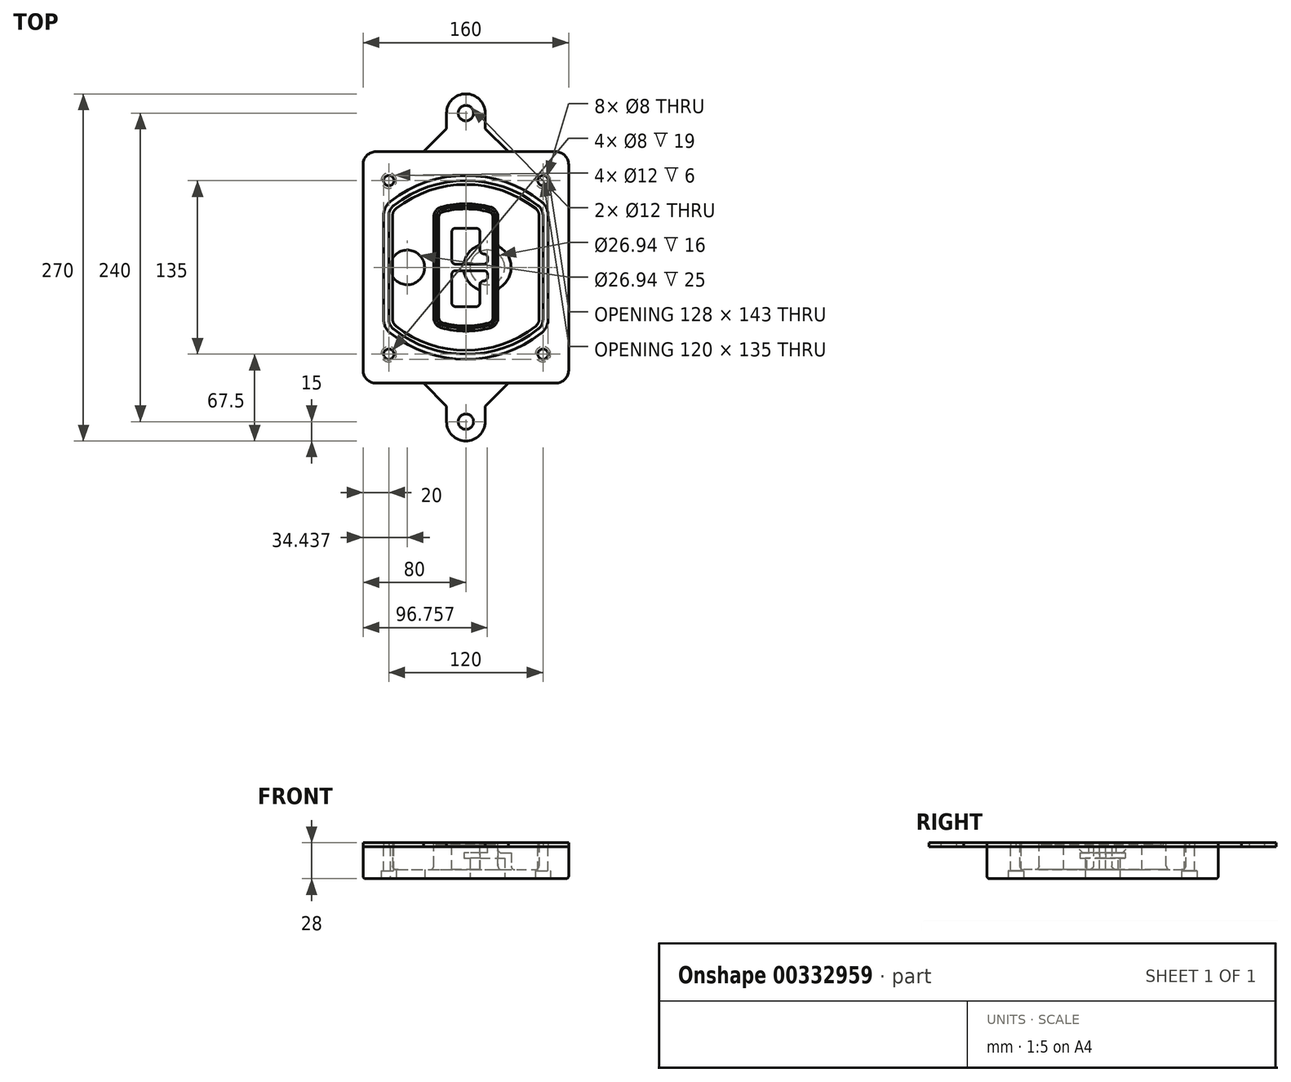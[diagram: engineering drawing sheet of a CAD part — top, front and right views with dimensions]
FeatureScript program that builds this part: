
annotation { "Feature Type Name" : "Feature", "Feature Type Description" : "" }
export const myFeature = defineFeature(function(context is Context, id is Id, definition is map)
    precondition{}
    {
        {
            var Q0;
            Q0=qCreatedBy(makeId("Top.planeOp"),FACE);
            var sketch = newSketch(context, id + "F0", { "sketchPlane" : qUnion([Q0])});
            skPoint(sketch, "E0.rect.middle", {"position": v(0, 0) * mm});
            skLineSegment(sketch, "E1.bottom", {"start": v(-70, -90) * mm, "end": v(70, -90) * mm});
            skLineSegment(sketch, "E1.top", {"start": v(-70, 90) * mm, "end": v(70, 90) * mm});
            skLineSegment(sketch, "E1.left", {"start": v(-80, -80) * mm, "end": v(-80, 80) * mm});
            skLineSegment(sketch, "E1.right", {"start": v(80, -80) * mm, "end": v(80, 80) * mm});
            skLineSegment(sketch, "E2", {"start": v(-80, 90) * mm, "end": v(80, -90) * mm, "construction": true});
            skLineSegment(sketch, "E3", {"start": v(80, 90) * mm, "end": v(-80, -90) * mm, "construction": true});
            skCircle(sketch, "E4", {"center": v(-60, 67.5) * mm, "radius": 4 * mm});
            skCircle(sketch, "E5", {"center": v(60, 67.5) * mm, "radius": 4 * mm});
            skCircle(sketch, "E6", {"center": v(60, -67.5) * mm, "radius": 4 * mm});
            skCircle(sketch, "E7", {"center": v(-60, -67.5) * mm, "radius": 4 * mm});
            skLineSegment(sketch, "E8", {"start": v(-60, 67.5) * mm, "end": v(60, 67.5) * mm, "construction": true});
            skLineSegment(sketch, "E9", {"start": v(60, 67.5) * mm, "end": v(60, -67.5) * mm, "construction": true});
            skLineSegment(sketch, "E10", {"start": v(60, -67.5) * mm, "end": v(-60, -67.5) * mm, "construction": true});
            skLineSegment(sketch, "E11", {"start": v(-60, -67.5) * mm, "end": v(-60, 67.5) * mm, "construction": true});
            skLineSegment(sketch, "E12", {"start": v(-60, 40.3) * mm, "end": v(-60, -40.3) * mm});
            skLineSegment(sketch, "E13", {"start": v(60, 40.3) * mm, "end": v(60, -40.3) * mm});
            skArc(sketch, "E14", {"start": v(56.15, 48.18) * mm, "mid": v(0, 67.5) * mm, "end": v(-56.15, 48.18) * mm});
            skArc(sketch, "E15", {"start": v(-56.15, -48.18) * mm, "mid": v(0, -67.5) * mm, "end": v(56.15, -48.18) * mm});
            skLineSegment(sketch, "E16", {"start": v(-60, 0) * mm, "end": v(60, 0) * mm, "construction": true});
            skPoint(sketch, "E17.visualSharp", {"position": v(-60, -45) * mm});
            skArc(sketch, "E17.filletArc", {"start": v(-60, -40.3) * mm, "mid": v(-58.99, -44.68) * mm, "end": v(-56.15, -48.18) * mm});
            skPoint(sketch, "E18.visualSharp", {"position": v(-60, 45) * mm});
            skArc(sketch, "E18.filletArc", {"start": v(-56.15, 48.18) * mm, "mid": v(-58.99, 44.68) * mm, "end": v(-60, 40.3) * mm});
            skPoint(sketch, "E19.visualSharp", {"position": v(60, 45) * mm});
            skArc(sketch, "E19.filletArc", {"start": v(60, 40.3) * mm, "mid": v(58.99, 44.68) * mm, "end": v(56.15, 48.18) * mm});
            skPoint(sketch, "E20.visualSharp", {"position": v(60, -45) * mm});
            skArc(sketch, "E20.filletArc", {"start": v(56.15, -48.18) * mm, "mid": v(58.99, -44.68) * mm, "end": v(60, -40.3) * mm});
            skPoint(sketch, "E21.visualSharp", {"position": v(-80, 90) * mm});
            skArc(sketch, "E21.filletArc", {"start": v(-70, 90) * mm, "mid": v(-77.07, 87.07) * mm, "end": v(-80, 80) * mm});
            skPoint(sketch, "E22.visualSharp", {"position": v(80, 90) * mm});
            skArc(sketch, "E22.filletArc", {"start": v(80, 80) * mm, "mid": v(77.07, 87.07) * mm, "end": v(70, 90) * mm});
            skPoint(sketch, "E23.visualSharp", {"position": v(80, -90) * mm});
            skArc(sketch, "E23.filletArc", {"start": v(70, -90) * mm, "mid": v(77.07, -87.07) * mm, "end": v(80, -80) * mm});
            skPoint(sketch, "E24.visualSharp", {"position": v(-80, -90) * mm});
            skArc(sketch, "E24.filletArc", {"start": v(-80, -80) * mm, "mid": v(-77.07, -87.07) * mm, "end": v(-70, -90) * mm});
            skArc(sketch, "E25.0", {"start": v(57, 40.3) * mm, "mid": v(56.3, 43.36) * mm, "end": v(54.3, 45.81) * mm});
            skLineSegment(sketch, "E25.1", {"start": v(57, 40.3) * mm, "end": v(57, -40.3) * mm});
            skArc(sketch, "E25.2", {"start": v(54.3, -45.81) * mm, "mid": v(56.3, -43.36) * mm, "end": v(57, -40.3) * mm});
            skArc(sketch, "E25.3", {"start": v(-54.3, -45.81) * mm, "mid": v(0, -64.5) * mm, "end": v(54.3, -45.81) * mm});
            skArc(sketch, "E25.4", {"start": v(-57, -40.3) * mm, "mid": v(-56.3, -43.36) * mm, "end": v(-54.3, -45.81) * mm});
            skArc(sketch, "E25.5", {"start": v(54.3, 45.81) * mm, "mid": v(0, 64.5) * mm, "end": v(-54.3, 45.81) * mm});
            skLineSegment(sketch, "E25.6", {"start": v(-57, 40.3) * mm, "end": v(-57, -40.3) * mm});
            skArc(sketch, "E25.7", {"start": v(-54.3, 45.81) * mm, "mid": v(-56.3, 43.36) * mm, "end": v(-57, 40.3) * mm});
            skArc(sketch, "E26.0", {"start": v(-58.62, 51.33) * mm, "mid": v(-62.58, 46.43) * mm, "end": v(-64, 40.3) * mm});
            skArc(sketch, "E26.1", {"start": v(58.62, 51.33) * mm, "mid": v(0, 71.5) * mm, "end": v(-58.62, 51.33) * mm});
            skArc(sketch, "E26.2", {"start": v(64, 40.3) * mm, "mid": v(62.58, 46.43) * mm, "end": v(58.62, 51.33) * mm});
            skLineSegment(sketch, "E26.3", {"start": v(64, 40.3) * mm, "end": v(64, -40.3) * mm});
            skArc(sketch, "E26.4", {"start": v(58.62, -51.33) * mm, "mid": v(62.58, -46.43) * mm, "end": v(64, -40.3) * mm});
            skLineSegment(sketch, "E26.5", {"start": v(-64, 40.3) * mm, "end": v(-64, -40.3) * mm});
            skArc(sketch, "E26.6", {"start": v(-58.62, -51.33) * mm, "mid": v(0, -71.5) * mm, "end": v(58.62, -51.33) * mm});
            skArc(sketch, "E26.7", {"start": v(-64, -40.3) * mm, "mid": v(-62.58, -46.43) * mm, "end": v(-58.62, -51.33) * mm});
            skSolve(sketch);
        }
        {
            var Q0;
            Q0=makeQuery(id+"F0.imprint","IMPRINT",FACE,{"disambiguationData":[TD([[makeQuery(id+"F0.imprint","IMPRINT",EDGE,{"derivedFrom":sQuery(id+"F0.wireOp",EDGE,"E1.bottom")}),1.0]])]});
            var Q1;
            Q1=makeQuery(id+"F0.imprint","IMPRINT",FACE,{"disambiguationData":[TD([[makeQuery(id+"F0.imprint","IMPRINT",EDGE,{"derivedFrom":sQuery(id+"F0.wireOp",EDGE,"E12")}),1.0]])]});
            var Q2;
            Q2=makeQuery(id+"F0.imprint","IMPRINT",FACE,{"disambiguationData":[TD([[makeQuery(id+"F0.imprint","IMPRINT",EDGE,{"derivedFrom":sQuery(id+"F0.wireOp",EDGE,"E25.0")}),1.0]])]});
            var Q3;
            Q3=makeQuery(id+"F0.imprint","IMPRINT",FACE,{"disambiguationData":[TD([[makeQuery(id+"F0.imprint","IMPRINT",EDGE,{"derivedFrom":sQuery(id+"F0.wireOp",EDGE,"E12")}),-1.0]])]});
            extrude(context, id + "F1", {"entities" : qUnion([Q0, Q1, Q2, Q3]), "oppositeDirection" : true, "depth" : 25 * mm});
        }
        {
            var Q0;
            Q0=makeQuery(id+"F0.imprint","IMPRINT",FACE,{"disambiguationData":[TD([[makeQuery(id+"F0.imprint","IMPRINT",EDGE,{"derivedFrom":sQuery(id+"F0.wireOp",EDGE,"E12")}),1.0]])]});
            extrude(context, id + "F2", {"entities" : qUnion([Q0]), "operationType" : NewBodyOperationType.ADD, "depth" : 3 * mm});
        }
        {
            var Q0;
            Q0=makeQuery(id+"F0.imprint","IMPRINT",FACE,{"disambiguationData":[TD([[makeQuery(id+"F0.imprint","IMPRINT",EDGE,{"derivedFrom":sQuery(id+"F0.wireOp",EDGE,"E25.0")}),1.0]])]});
            extrude(context, id + "F3", {"entities" : qUnion([Q0]), "operationType" : NewBodyOperationType.REMOVE, "oppositeDirection" : true, "depth" : 18 * mm});
        }
        {
            var Q0;
            Q0=makeQuery(id+"F2.opExtrude","CAP_FACE",FACE,{"disambiguationData":[OSD([sQuery(id+"F0.wireOp",EDGE,"E12"),sQuery(id+"F0.wireOp",EDGE,"E13"),sQuery(id+"F0.wireOp",EDGE,"E14"),sQuery(id+"F0.wireOp",EDGE,"E15"),sQuery(id+"F0.wireOp",EDGE,"E17.filletArc"),sQuery(id+"F0.wireOp",EDGE,"E18.filletArc"),sQuery(id+"F0.wireOp",EDGE,"E19.filletArc"),sQuery(id+"F0.wireOp",EDGE,"E20.filletArc"),sQuery(id+"F0.wireOp",EDGE,"E25.0"),sQuery(id+"F0.wireOp",EDGE,"E25.1"),sQuery(id+"F0.wireOp",EDGE,"E25.2"),sQuery(id+"F0.wireOp",EDGE,"E25.3"),sQuery(id+"F0.wireOp",EDGE,"E25.4"),sQuery(id+"F0.wireOp",EDGE,"E25.5"),sQuery(id+"F0.wireOp",EDGE,"E25.6"),sQuery(id+"F0.wireOp",EDGE,"E25.7")])],"isStart":false});
            var sketch = newSketch(context, id + "F4", { "sketchPlane" : qUnion([Q0])});
            skArc(sketch, "E27.0", {"start": v(-19.08, -46.97) * mm, "mid": v(0, -49.5) * mm, "end": v(19.08, -46.97) * mm});
            skArc(sketch, "E28.0", {"start": v(19.08, 46.97) * mm, "mid": v(0, 49.5) * mm, "end": v(-19.08, 46.97) * mm});
            skLineSegment(sketch, "E29", {"start": v(-25, 39.25) * mm, "end": v(-25, -39.25) * mm});
            skLineSegment(sketch, "E30", {"start": v(25, 39.25) * mm, "end": v(25, -39.25) * mm});
            skLineSegment(sketch, "E31", {"start": v(-25, 45.1) * mm, "end": v(25, 45.1) * mm, "construction": true});
            skLineSegment(sketch, "E32", {"start": v(-25, -45.1) * mm, "end": v(25, -45.1) * mm, "construction": true});
            skPoint(sketch, "E33.visualSharp", {"position": v(-25, 45.1) * mm});
            skArc(sketch, "E33.filletArc", {"start": v(-19.08, 46.97) * mm, "mid": v(-23.35, 44.11) * mm, "end": v(-25, 39.25) * mm});
            skPoint(sketch, "E34.visualSharp", {"position": v(25, 45.1) * mm});
            skArc(sketch, "E34.filletArc", {"start": v(25, 39.25) * mm, "mid": v(23.35, 44.11) * mm, "end": v(19.08, 46.97) * mm});
            skPoint(sketch, "E35.visualSharp", {"position": v(25, -45.1) * mm});
            skArc(sketch, "E35.filletArc", {"start": v(19.08, -46.97) * mm, "mid": v(23.35, -44.11) * mm, "end": v(25, -39.25) * mm});
            skPoint(sketch, "E36.visualSharp", {"position": v(-25, -45.1) * mm});
            skArc(sketch, "E36.filletArc", {"start": v(-25, -39.25) * mm, "mid": v(-23.35, -44.11) * mm, "end": v(-19.08, -46.97) * mm});
            skArc(sketch, "E37.0", {"start": v(54.3, 45.81) * mm, "mid": v(0, 64.5) * mm, "end": v(-54.3, 45.81) * mm});
            skArc(sketch, "E37.1", {"start": v(-54.3, 45.81) * mm, "mid": v(-56.3, 43.36) * mm, "end": v(-57, 40.3) * mm});
            skLineSegment(sketch, "E37.2", {"start": v(-57, 40.3) * mm, "end": v(-57, -40.3) * mm});
            skArc(sketch, "E37.3", {"start": v(-57, -40.3) * mm, "mid": v(-56.3, -43.36) * mm, "end": v(-54.3, -45.81) * mm});
            skArc(sketch, "E37.4", {"start": v(-54.3, -45.81) * mm, "mid": v(0, -64.5) * mm, "end": v(54.3, -45.81) * mm});
            skArc(sketch, "E37.5", {"start": v(54.3, -45.81) * mm, "mid": v(56.3, -43.36) * mm, "end": v(57, -40.3) * mm});
            skLineSegment(sketch, "E37.6", {"start": v(57, 40.3) * mm, "end": v(57, -40.3) * mm});
            skArc(sketch, "E37.7", {"start": v(57, 40.3) * mm, "mid": v(56.3, 43.36) * mm, "end": v(54.3, 45.81) * mm});
            skLineSegment(sketch, "E38.0", {"start": v(23, 39.25) * mm, "end": v(23, -39.25) * mm});
            skArc(sketch, "E38.1", {"start": v(18.56, -45.04) * mm, "mid": v(21.76, -42.9) * mm, "end": v(23, -39.25) * mm});
            skArc(sketch, "E38.2", {"start": v(-18.56, -45.04) * mm, "mid": v(0, -47.5) * mm, "end": v(18.56, -45.04) * mm});
            skArc(sketch, "E38.3", {"start": v(-23, -39.25) * mm, "mid": v(-21.76, -42.9) * mm, "end": v(-18.56, -45.04) * mm});
            skLineSegment(sketch, "E38.4", {"start": v(-23, 39.25) * mm, "end": v(-23, -39.25) * mm});
            skArc(sketch, "E38.5", {"start": v(23, 39.25) * mm, "mid": v(21.76, 42.9) * mm, "end": v(18.56, 45.04) * mm});
            skArc(sketch, "E38.6", {"start": v(-18.56, 45.04) * mm, "mid": v(-21.76, 42.9) * mm, "end": v(-23, 39.25) * mm});
            skArc(sketch, "E38.7", {"start": v(18.56, 45.04) * mm, "mid": v(0, 47.5) * mm, "end": v(-18.56, 45.04) * mm});
            skArc(sketch, "E39.0", {"start": v(21, 39.25) * mm, "mid": v(20.18, 41.68) * mm, "end": v(18.04, 43.1) * mm});
            skLineSegment(sketch, "E39.1", {"start": v(21, 39.25) * mm, "end": v(21, -39.25) * mm});
            skArc(sketch, "E39.2", {"start": v(18.04, -43.1) * mm, "mid": v(20.18, -41.68) * mm, "end": v(21, -39.25) * mm});
            skArc(sketch, "E39.3", {"start": v(-18.04, -43.1) * mm, "mid": v(0, -45.5) * mm, "end": v(18.04, -43.1) * mm});
            skArc(sketch, "E39.4", {"start": v(-21, -39.25) * mm, "mid": v(-20.18, -41.68) * mm, "end": v(-18.04, -43.1) * mm});
            skArc(sketch, "E39.5", {"start": v(18.04, 43.1) * mm, "mid": v(0, 45.5) * mm, "end": v(-18.04, 43.1) * mm});
            skLineSegment(sketch, "E39.6", {"start": v(-21, 39.25) * mm, "end": v(-21, -39.25) * mm});
            skArc(sketch, "E39.7", {"start": v(-18.04, 43.1) * mm, "mid": v(-20.18, 41.68) * mm, "end": v(-21, 39.25) * mm});
            skLineSegment(sketch, "E40", {"start": v(-25, 0) * mm, "end": v(25, 0) * mm, "construction": true});
            skLineSegment(sketch, "E41", {"start": v(-11, 5.5) * mm, "end": v(-11, 27.5) * mm});
            skLineSegment(sketch, "E42", {"start": v(-8, 30.5) * mm, "end": v(8, 30.5) * mm});
            skLineSegment(sketch, "E43", {"start": v(11, 27.5) * mm, "end": v(11, 13.5) * mm});
            skLineSegment(sketch, "E44", {"start": v(14, 10.5) * mm, "end": v(14, 10.5) * mm});
            skLineSegment(sketch, "E45", {"start": v(17, 7.5) * mm, "end": v(17, 5.5) * mm});
            skLineSegment(sketch, "E46", {"start": v(14, 2.5) * mm, "end": v(-8, 2.5) * mm});
            skPoint(sketch, "E47.visualSharp", {"position": v(-11, 30.5) * mm});
            skArc(sketch, "E47.filletArc", {"start": v(-8, 30.5) * mm, "mid": v(-10.12, 29.62) * mm, "end": v(-11, 27.5) * mm});
            skPoint(sketch, "E48.visualSharp", {"position": v(11, 30.5) * mm});
            skArc(sketch, "E48.filletArc", {"start": v(11, 27.5) * mm, "mid": v(10.12, 29.62) * mm, "end": v(8, 30.5) * mm});
            skPoint(sketch, "E49.visualSharp", {"position": v(11, 10.5) * mm});
            skArc(sketch, "E49.filletArc", {"start": v(11, 13.5) * mm, "mid": v(11.88, 11.38) * mm, "end": v(14, 10.5) * mm});
            skPoint(sketch, "E50.visualSharp", {"position": v(17, 10.5) * mm});
            skArc(sketch, "E50.filletArc", {"start": v(17, 7.5) * mm, "mid": v(16.12, 9.62) * mm, "end": v(14, 10.5) * mm});
            skPoint(sketch, "E51.visualSharp", {"position": v(17, 2.5) * mm});
            skArc(sketch, "E51.filletArc", {"start": v(14, 2.5) * mm, "mid": v(16.12, 3.38) * mm, "end": v(17, 5.5) * mm});
            skPoint(sketch, "E52.visualSharp", {"position": v(-11, 2.5) * mm});
            skArc(sketch, "E52.filletArc", {"start": v(-11, 5.5) * mm, "mid": v(-10.12, 3.38) * mm, "end": v(-8, 2.5) * mm});
            skLineSegment(sketch, "E53.0.MirrorCS", {"start": v(14, -2.5) * mm, "end": v(-8, -2.5) * mm});
            skArc(sketch, "E54.0.MirrorCS", {"start": v(-11, -5.5) * mm, "mid": v(-10.12, -3.38) * mm, "end": v(-8, -2.5) * mm});
            skLineSegment(sketch, "E55.0.MirrorCS", {"start": v(-11, -5.5) * mm, "end": v(-11, -27.5) * mm});
            skArc(sketch, "E56.0.MirrorCS", {"start": v(-8, -30.5) * mm, "mid": v(-10.12, -29.62) * mm, "end": v(-11, -27.5) * mm});
            skLineSegment(sketch, "E57.0.MirrorCS", {"start": v(-8, -30.5) * mm, "end": v(8, -30.5) * mm});
            skArc(sketch, "E58.0.MirrorCS", {"start": v(11, -27.5) * mm, "mid": v(10.12, -29.62) * mm, "end": v(8, -30.5) * mm});
            skLineSegment(sketch, "E59.0.MirrorCS", {"start": v(11, -27.5) * mm, "end": v(11, -13.5) * mm});
            skArc(sketch, "E60.0.MirrorCS", {"start": v(11, -13.5) * mm, "mid": v(11.88, -11.38) * mm, "end": v(14, -10.5) * mm});
            skArc(sketch, "E61.0.MirrorCS", {"start": v(17, -7.5) * mm, "mid": v(16.12, -9.62) * mm, "end": v(14, -10.5) * mm});
            skLineSegment(sketch, "E62.0.MirrorCS", {"start": v(17, -7.5) * mm, "end": v(17, -5.5) * mm});
            skArc(sketch, "E63.0.MirrorCS", {"start": v(14, -2.5) * mm, "mid": v(16.12, -3.38) * mm, "end": v(17, -5.5) * mm});
            skSolve(sketch);
        }
        {
            var Q0;
            Q0=makeQuery(id+"F4.imprint","IMPRINT",FACE,{"disambiguationData":[TD([[makeQuery(id+"F4.imprint","IMPRINT",EDGE,{"derivedFrom":sQuery(id+"F4.wireOp",EDGE,"E27.0")}),1.0]])]});
            var Q1;
            Q1=makeQuery(id+"F4.imprint","IMPRINT",FACE,{"disambiguationData":[TD([[makeQuery(id+"F4.imprint","IMPRINT",EDGE,{"derivedFrom":sQuery(id+"F4.wireOp",EDGE,"E38.0")}),-1.0]])]});
            var Q2;
            Q2=makeQuery(id+"F4.imprint","IMPRINT",FACE,{"disambiguationData":[TD([[makeQuery(id+"F4.imprint","IMPRINT",EDGE,{"derivedFrom":sQuery(id+"F4.wireOp",EDGE,"E39.0")}),1.0]])]});
            extrude(context, id + "F5", {"entities" : qUnion([Q0, Q1, Q2]), "operationType" : NewBodyOperationType.ADD, "endBound" : BoundingType.UP_TO_NEXT, "oppositeDirection" : true, "depth" : 25 * mm});
        }
        {
            var Q0;
            Q0=makeQuery(id+"F4.imprint","IMPRINT",FACE,{"disambiguationData":[TD([[makeQuery(id+"F4.imprint","IMPRINT",EDGE,{"derivedFrom":sQuery(id+"F4.wireOp",EDGE,"E38.0")}),-1.0]])]});
            extrude(context, id + "F6", {"entities" : qUnion([Q0]), "operationType" : NewBodyOperationType.REMOVE, "oppositeDirection" : true, "depth" : 2 * mm});
        }
        {
            var Q0;
            Q0=makeQuery(id+"F1.opExtrude","CAP_FACE",FACE,{"disambiguationData":[OSD([sQuery(id+"F0.wireOp",EDGE,"E1.bottom"),sQuery(id+"F0.wireOp",EDGE,"E1.top"),sQuery(id+"F0.wireOp",EDGE,"E1.left"),sQuery(id+"F0.wireOp",EDGE,"E1.right"),sQuery(id+"F0.wireOp",EDGE,"E4"),sQuery(id+"F0.wireOp",EDGE,"E5"),sQuery(id+"F0.wireOp",EDGE,"E6"),sQuery(id+"F0.wireOp",EDGE,"E7"),sQuery(id+"F0.wireOp",EDGE,"E21.filletArc"),sQuery(id+"F0.wireOp",EDGE,"E22.filletArc"),sQuery(id+"F0.wireOp",EDGE,"E23.filletArc"),sQuery(id+"F0.wireOp",EDGE,"E24.filletArc")])],"isStart":false});
            var sketch = newSketch(context, id + "F7", { "sketchPlane" : qUnion([Q0])});
            skCircle(sketch, "E64", {"center": v(16.76, 0) * mm, "radius": 13.47 * mm});
            skCircle(sketch, "E65", {"center": v(-45.56, 0) * mm, "radius": 13.47 * mm});
            skLineSegment(sketch, "E66", {"start": v(80, 0) * mm, "end": v(-80, 0) * mm});
            skCircle(sketch, "E67", {"center": v(16.76, 0) * mm, "radius": 18.47 * mm});
            skCircle(sketch, "E68", {"center": v(60, -67.5) * mm, "radius": 6 * mm});
            skCircle(sketch, "E69", {"center": v(-60, -67.5) * mm, "radius": 6 * mm});
            skCircle(sketch, "E70", {"center": v(-60, 67.5) * mm, "radius": 6 * mm});
            skCircle(sketch, "E71", {"center": v(60, 67.5) * mm, "radius": 6 * mm});
            skSolve(sketch);
        }
        {
            var Q0;
            {var subQ1=sQuery(id+"F7.wireOp",EDGE,"E66");var subQ4=sQuery(id+"F7.wireOp",EDGE,"E64");var subQ6=makeQuery(id+"F7.imprint","INTERSECT",VERTEX,{"disambiguationData":[OD(0.0)],"derivedFrom":[subQ4,subQ1]});Q0=makeQuery(id+"F7.imprint","IMPRINT",FACE,{"disambiguationData":[TD([[makeQuery(id+"F7.imprint","IMPRINT",EDGE,{"disambiguationData":[TD([[subQ6,-1.0]])],"derivedFrom":subQ4}),-1.0]])]});}
            var Q1;
            {var subQ0=sQuery(id+"F7.wireOp",EDGE,"E66");var subQ1=sQuery(id+"F7.wireOp",EDGE,"E64");var subQ3=makeQuery(id+"F7.imprint","INTERSECT",VERTEX,{"disambiguationData":[OD(0.0)],"derivedFrom":[subQ1,subQ0]});Q1=makeQuery(id+"F7.imprint","IMPRINT",FACE,{"disambiguationData":[TD([[makeQuery(id+"F7.imprint","IMPRINT",EDGE,{"disambiguationData":[TD([[subQ3,-1.0]])],"derivedFrom":subQ1}),1.0]])]});}
            var Q2;
            {var subQ0=sQuery(id+"F7.wireOp",EDGE,"E66");var subQ1=sQuery(id+"F7.wireOp",EDGE,"E64");var subQ3=makeQuery(id+"F7.imprint","INTERSECT",VERTEX,{"disambiguationData":[OD(0.0)],"derivedFrom":[subQ1,subQ0]});Q2=makeQuery(id+"F7.imprint","IMPRINT",FACE,{"disambiguationData":[TD([[makeQuery(id+"F7.imprint","IMPRINT",EDGE,{"disambiguationData":[TD([[subQ3,1.0]])],"derivedFrom":subQ1}),1.0]])]});}
            var Q3;
            {var subQ1=sQuery(id+"F7.wireOp",EDGE,"E66");var subQ4=sQuery(id+"F7.wireOp",EDGE,"E64");var subQ6=makeQuery(id+"F7.imprint","INTERSECT",VERTEX,{"disambiguationData":[OD(0.0)],"derivedFrom":[subQ4,subQ1]});Q3=makeQuery(id+"F7.imprint","IMPRINT",FACE,{"disambiguationData":[TD([[makeQuery(id+"F7.imprint","IMPRINT",EDGE,{"disambiguationData":[TD([[subQ6,1.0]])],"derivedFrom":subQ4}),-1.0]])]});}
            extrude(context, id + "F8", {"entities" : qUnion([Q0, Q1, Q2, Q3]), "operationType" : NewBodyOperationType.ADD, "oppositeDirection" : true, "depth" : 20 * mm});
        }
        {
            var Q0;
            {var subQ0=sQuery(id+"F7.wireOp",EDGE,"E66");var subQ1=sQuery(id+"F7.wireOp",EDGE,"E64");var subQ3=makeQuery(id+"F7.imprint","INTERSECT",VERTEX,{"disambiguationData":[OD(0.0)],"derivedFrom":[subQ1,subQ0]});Q0=makeQuery(id+"F7.imprint","IMPRINT",FACE,{"disambiguationData":[TD([[makeQuery(id+"F7.imprint","IMPRINT",EDGE,{"disambiguationData":[TD([[subQ3,-1.0]])],"derivedFrom":subQ1}),1.0]])]});}
            var Q1;
            {var subQ0=sQuery(id+"F7.wireOp",EDGE,"E66");var subQ1=sQuery(id+"F7.wireOp",EDGE,"E64");var subQ3=makeQuery(id+"F7.imprint","INTERSECT",VERTEX,{"disambiguationData":[OD(0.0)],"derivedFrom":[subQ1,subQ0]});Q1=makeQuery(id+"F7.imprint","IMPRINT",FACE,{"disambiguationData":[TD([[makeQuery(id+"F7.imprint","IMPRINT",EDGE,{"disambiguationData":[TD([[subQ3,1.0]])],"derivedFrom":subQ1}),1.0]])]});}
            extrude(context, id + "F9", {"entities" : qUnion([Q0, Q1]), "operationType" : NewBodyOperationType.REMOVE, "oppositeDirection" : true, "depth" : 16 * mm});
        }
        {
            var Q0;
            {var subQ0=sQuery(id+"F7.wireOp",EDGE,"E66");var subQ1=sQuery(id+"F7.wireOp",EDGE,"E65");var subQ3=makeQuery(id+"F7.imprint","INTERSECT",VERTEX,{"disambiguationData":[OD(0.0)],"derivedFrom":[subQ1,subQ0]});Q0=makeQuery(id+"F7.imprint","IMPRINT",FACE,{"disambiguationData":[TD([[makeQuery(id+"F7.imprint","IMPRINT",EDGE,{"disambiguationData":[TD([[subQ3,-1.0]])],"derivedFrom":subQ1}),1.0]])]});}
            var Q1;
            {var subQ0=sQuery(id+"F7.wireOp",EDGE,"E66");var subQ1=sQuery(id+"F7.wireOp",EDGE,"E65");var subQ3=makeQuery(id+"F7.imprint","INTERSECT",VERTEX,{"disambiguationData":[OD(0.0)],"derivedFrom":[subQ1,subQ0]});Q1=makeQuery(id+"F7.imprint","IMPRINT",FACE,{"disambiguationData":[TD([[makeQuery(id+"F7.imprint","IMPRINT",EDGE,{"disambiguationData":[TD([[subQ3,1.0]])],"derivedFrom":subQ1}),1.0]])]});}
            extrude(context, id + "F10", {"entities" : qUnion([Q0, Q1]), "operationType" : NewBodyOperationType.REMOVE, "oppositeDirection" : true, "depth" : 25 * mm});
        }
        {
            var Q0;
            Q0=makeQuery(id+"F7.imprint","IMPRINT",FACE,{"disambiguationData":[TD([[makeQuery(id+"F7.imprint","IMPRINT",EDGE,{"derivedFrom":sQuery(id+"F7.wireOp",EDGE,"E68")}),1.0]])]});
            var Q1;
            Q1=makeQuery(id+"F7.imprint","IMPRINT",FACE,{"disambiguationData":[TD([[makeQuery(id+"F7.imprint","IMPRINT",EDGE,{"derivedFrom":makeQuery(id+"F1.opExtrude","CAP_EDGE",EDGE,{"disambiguationData":[OSD([sQuery(id+"F0.wireOp",EDGE,"E5")])],"isStart":false})}),-1.0]])]});
            var Q2;
            Q2=makeQuery(id+"F7.imprint","IMPRINT",FACE,{"disambiguationData":[TD([[makeQuery(id+"F7.imprint","IMPRINT",EDGE,{"derivedFrom":sQuery(id+"F7.wireOp",EDGE,"E69")}),1.0]])]});
            var Q3;
            Q3=makeQuery(id+"F7.imprint","IMPRINT",FACE,{"disambiguationData":[TD([[makeQuery(id+"F7.imprint","IMPRINT",EDGE,{"derivedFrom":makeQuery(id+"F1.opExtrude","CAP_EDGE",EDGE,{"disambiguationData":[OSD([sQuery(id+"F0.wireOp",EDGE,"E4")])],"isStart":false})}),-1.0]])]});
            var Q4;
            Q4=makeQuery(id+"F7.imprint","IMPRINT",FACE,{"disambiguationData":[TD([[makeQuery(id+"F7.imprint","IMPRINT",EDGE,{"derivedFrom":sQuery(id+"F7.wireOp",EDGE,"E70")}),1.0]])]});
            var Q5;
            Q5=makeQuery(id+"F7.imprint","IMPRINT",FACE,{"disambiguationData":[TD([[makeQuery(id+"F7.imprint","IMPRINT",EDGE,{"derivedFrom":makeQuery(id+"F1.opExtrude","CAP_EDGE",EDGE,{"disambiguationData":[OSD([sQuery(id+"F0.wireOp",EDGE,"E7")])],"isStart":false})}),-1.0]])]});
            var Q6;
            Q6=makeQuery(id+"F7.imprint","IMPRINT",FACE,{"disambiguationData":[TD([[makeQuery(id+"F7.imprint","IMPRINT",EDGE,{"derivedFrom":sQuery(id+"F7.wireOp",EDGE,"E71")}),1.0]])]});
            var Q7;
            Q7=makeQuery(id+"F7.imprint","IMPRINT",FACE,{"disambiguationData":[TD([[makeQuery(id+"F7.imprint","IMPRINT",EDGE,{"derivedFrom":makeQuery(id+"F1.opExtrude","CAP_EDGE",EDGE,{"disambiguationData":[OSD([sQuery(id+"F0.wireOp",EDGE,"E6")])],"isStart":false})}),-1.0]])]});
            extrude(context, id + "F11", {"entities" : qUnion([Q0, Q1, Q2, Q3, Q4, Q5, Q6, Q7]), "operationType" : NewBodyOperationType.REMOVE, "oppositeDirection" : true, "depth" : 6 * mm});
        }
        {
            var Q0;
            Q0=makeQuery(id+"F9.boolean.opBoolean","COPY",FACE,{"derivedFrom":makeQuery(id+"F9.opExtrude","CAP_FACE",FACE,{"disambiguationData":[OSD([sQuery(id+"F7.wireOp",EDGE,"E64")])],"isStart":false})});
            var sketch = newSketch(context, id + "F12", { "sketchPlane" : qUnion([Q0])});
            skArc(sketch, "E72.0", {"start": v(11, 17.55) * mm, "mid": v(2.57, 11.82) * mm, "end": v(-1.54, 2.5) * mm});
            skArc(sketch, "E72.1", {"start": v(-1.54, -2.5) * mm, "mid": v(2.57, -11.82) * mm, "end": v(11, -17.55) * mm});
            skLineSegment(sketch, "E73", {"start": v(-1.54, -2.5) * mm, "end": v(14, -2.5) * mm});
            skLineSegment(sketch, "E74.0", {"start": v(14, 2.5) * mm, "end": v(-1.54, 2.5) * mm});
            skArc(sketch, "E74.1", {"start": v(14, 2.5) * mm, "mid": v(16.12, 3.38) * mm, "end": v(17, 5.5) * mm});
            skLineSegment(sketch, "E74.2", {"start": v(17, 7.5) * mm, "end": v(17, 5.5) * mm});
            skArc(sketch, "E74.3", {"start": v(17, 7.5) * mm, "mid": v(16.12, 9.62) * mm, "end": v(14, 10.5) * mm});
            skArc(sketch, "E74.4", {"start": v(11, 13.5) * mm, "mid": v(11.88, 11.38) * mm, "end": v(14, 10.5) * mm});
            skLineSegment(sketch, "E74.5", {"start": v(11, 17.55) * mm, "end": v(11, 13.5) * mm});
            skLineSegment(sketch, "E74.7", {"start": v(14, -2.5) * mm, "end": v(-1.54, -2.5) * mm});
            skArc(sketch, "E74.8", {"start": v(14, -2.5) * mm, "mid": v(16.12, -3.38) * mm, "end": v(17, -5.5) * mm});
            skLineSegment(sketch, "E74.9", {"start": v(17, -7.5) * mm, "end": v(17, -5.5) * mm});
            skArc(sketch, "E74.10", {"start": v(17, -7.5) * mm, "mid": v(16.12, -9.62) * mm, "end": v(14, -10.5) * mm});
            skArc(sketch, "E74.11", {"start": v(11, -13.5) * mm, "mid": v(11.88, -11.38) * mm, "end": v(14, -10.5) * mm});
            skLineSegment(sketch, "E74.12", {"start": v(11, -17.55) * mm, "end": v(11, -13.5) * mm});
            skPoint(sketch, "E75.orphan", {"position": v(11, -27.5) * mm});
            skPoint(sketch, "E76.orphan", {"position": v(-8, -2.5) * mm});
            skPoint(sketch, "E77.orphan", {"position": v(-8, 2.5) * mm});
            skPoint(sketch, "E78.orphan", {"position": v(11, 27.5) * mm});
            skSolve(sketch);
        }
        {
            var Q0;
            {var subQ7=sQuery(id+"F12.wireOp",EDGE,"E72.0");var subQ14=sQuery(id+"F12.wireOp",EDGE,"E72.1");var subQ16=sQuery(id+"F12.wireOp",EDGE,"E74.1");var subQ18=sQuery(id+"F12.wireOp",EDGE,"E74.8");Q0=qUnion([makeQuery(id+"F12.imprint","IMPRINT",FACE,{"disambiguationData":[TD([[makeQuery(id+"F12.imprint","IMPRINT",EDGE,{"derivedFrom":subQ7}),1.0]])]}),makeQuery(id+"F12.imprint","IMPRINT",FACE,{"disambiguationData":[TD([[makeQuery(id+"F12.imprint","IMPRINT",EDGE,{"derivedFrom":subQ14}),1.0]])]}),makeQuery(id+"F12.imprint","IMPRINT",FACE,{"disambiguationData":[TD([[makeQuery(id+"F12.imprint","IMPRINT",EDGE,{"derivedFrom":subQ16}),1.0]])]}),makeQuery(id+"F12.imprint","IMPRINT",FACE,{"disambiguationData":[TD([[makeQuery(id+"F12.imprint","IMPRINT",EDGE,{"derivedFrom":subQ18}),-1.0]])]})]);}
            var Q1;
            Q1=makeQuery(id+"F5.boolean.opBoolean","SPLIT",FACE,{"disambiguationData":[TD([makeQuery(id+"F5.opExtrude","SWEPT_FACE",FACE,{"disambiguationData":[OSD([sQuery(id+"F4.wireOp",EDGE,"E41")])]})])],"derivedFrom":makeQuery(id+"F3.boolean.opBoolean","COPY",FACE,{"derivedFrom":makeQuery(id+"F3.opExtrude","CAP_FACE",FACE,{"disambiguationData":[OSD([sQuery(id+"F0.wireOp",EDGE,"E25.0"),sQuery(id+"F0.wireOp",EDGE,"E25.1"),sQuery(id+"F0.wireOp",EDGE,"E25.2"),sQuery(id+"F0.wireOp",EDGE,"E25.3"),sQuery(id+"F0.wireOp",EDGE,"E25.4"),sQuery(id+"F0.wireOp",EDGE,"E25.5"),sQuery(id+"F0.wireOp",EDGE,"E25.6"),sQuery(id+"F0.wireOp",EDGE,"E25.7")])],"isStart":false})})});
            extrude(context, id + "F13", {"entities" : qUnion([Q0]), "operationType" : NewBodyOperationType.REMOVE, "endBound" : BoundingType.UP_TO_SURFACE, "endBoundEntityFace" : qUnion([Q1]), "depth" : 25 * mm});
        }
        {
            var Q0;
            Q0=makeQuery(id+"F3.boolean.opBoolean","COPY",EDGE,{"derivedFrom":makeQuery(id+"F3.opExtrude","CAP_EDGE",EDGE,{"disambiguationData":[OSD([sQuery(id+"F0.wireOp",EDGE,"E25.6")])],"isStart":false})});
            var Q1;
            Q1=makeQuery(id+"F8.boolean.opBoolean","INTERSECT",EDGE,{"derivedFrom":[makeQuery(id+"F5.opExtrude","SWEPT_FACE",FACE,{"disambiguationData":[OSD([sQuery(id+"F4.wireOp",EDGE,"E30")])]}),makeQuery(id+"F8.opExtrude","CAP_FACE",FACE,{"disambiguationData":[OSD([sQuery(id+"F7.wireOp",EDGE,"E67")])],"isStart":false})]});
            var Q2;
            Q2=makeQuery(id+"F8.boolean.opBoolean","INTERSECT",EDGE,{"disambiguationData":[OD(1.0)],"derivedFrom":[makeQuery(id+"F5.opExtrude","SWEPT_FACE",FACE,{"disambiguationData":[OSD([sQuery(id+"F4.wireOp",EDGE,"E30")])]}),makeQuery(id+"F8.opExtrude","SWEPT_FACE",FACE,{"disambiguationData":[OSD([sQuery(id+"F7.wireOp",EDGE,"E67")])]})]});
            var Q3;
            {var subQ0=sQuery(id+"F4.wireOp",EDGE,"E30");Q3=makeQuery(id+"F8.boolean.opBoolean","SPLIT",EDGE,{"disambiguationData":[TD([makeQuery(id+"F5.opExtrude","SWEPT_FACE",FACE,{"disambiguationData":[OSD([sQuery(id+"F4.wireOp",EDGE,"E35.filletArc")])]})])],"derivedFrom":makeQuery(id+"F5.opExtrude","CAP_EDGE",EDGE,{"disambiguationData":[OSD([subQ0])],"isStart":false})});}
            var Q4;
            {var subQ0=sQuery(id+"F0.wireOp",EDGE,"E25.7");var subQ1=sQuery(id+"F0.wireOp",EDGE,"E25.1");var subQ2=sQuery(id+"F0.wireOp",EDGE,"E25.6");var subQ3=sQuery(id+"F0.wireOp",EDGE,"E25.5");var subQ4=sQuery(id+"F0.wireOp",EDGE,"E25.4");var subQ5=sQuery(id+"F0.wireOp",EDGE,"E25.0");var subQ6=sQuery(id+"F0.wireOp",EDGE,"E25.2");var subQ7=sQuery(id+"F0.wireOp",EDGE,"E25.3");Q4=makeQuery(id+"F8.boolean.opBoolean","INTERSECT",EDGE,{"derivedFrom":[makeQuery(id+"F5.boolean.opBoolean","SPLIT",FACE,{"disambiguationData":[TD([makeQuery(id+"F2.opExtrude","SWEPT_FACE",FACE,{"disambiguationData":[OSD([subQ5])]})])],"derivedFrom":makeQuery(id+"F3.boolean.opBoolean","COPY",FACE,{"derivedFrom":makeQuery(id+"F3.opExtrude","CAP_FACE",FACE,{"disambiguationData":[OSD([subQ5,subQ1,subQ6,subQ7,subQ4,subQ3,subQ2,subQ0])],"isStart":false})})}),makeQuery(id+"F8.opExtrude","SWEPT_FACE",FACE,{"disambiguationData":[OSD([sQuery(id+"F7.wireOp",EDGE,"E67")])]})]});}
            var Q5;
            Q5=makeQuery(id+"F8.boolean.opBoolean","INTERSECT",EDGE,{"disambiguationData":[OD(0.0)],"derivedFrom":[makeQuery(id+"F5.opExtrude","SWEPT_FACE",FACE,{"disambiguationData":[OSD([sQuery(id+"F4.wireOp",EDGE,"E30")])]}),makeQuery(id+"F8.opExtrude","SWEPT_FACE",FACE,{"disambiguationData":[OSD([sQuery(id+"F7.wireOp",EDGE,"E67")])]})]});
            fillet(context, id + "F14", {"entities" : qUnion([Q0, Q1, Q2, Q3, Q4, Q5]), "radius" : 3 * mm, "tangentPropagation" : true, "allowEdgeOverflow" : false});
        }
        {
            var Q0;
            Q0=makeQuery(id+"F1.opExtrude","CAP_EDGE",EDGE,{"disambiguationData":[OSD([sQuery(id+"F0.wireOp",EDGE,"E1.bottom")])],"isStart":false});
            fillet(context, id + "F15", {"entities" : qUnion([Q0]), "radius" : 2 * mm, "tangentPropagation" : true, "allowEdgeOverflow" : false});
        }
        {
            var Q0;
            {var subQ0=sQuery(id+"F0.wireOp",EDGE,"E21.filletArc");var subQ1=sQuery(id+"F0.wireOp",EDGE,"E7");var subQ2=sQuery(id+"F0.wireOp",EDGE,"E6");var subQ3=sQuery(id+"F0.wireOp",EDGE,"E5");var subQ4=sQuery(id+"F0.wireOp",EDGE,"E4");var subQ5=sQuery(id+"F0.wireOp",EDGE,"E22.filletArc");var subQ6=sQuery(id+"F0.wireOp",EDGE,"E1.bottom");var subQ7=sQuery(id+"F0.wireOp",EDGE,"E1.right");var subQ8=sQuery(id+"F0.wireOp",EDGE,"E1.top");var subQ9=sQuery(id+"F0.wireOp",EDGE,"E1.left");var subQ10=sQuery(id+"F0.wireOp",EDGE,"E23.filletArc");var subQ11=sQuery(id+"F0.wireOp",EDGE,"E24.filletArc");Q0=makeQuery(id+"F2.boolean.opBoolean","SPLIT",FACE,{"disambiguationData":[TD([makeQuery(id+"F1.opExtrude","SWEPT_FACE",FACE,{"disambiguationData":[OSD([subQ6])]})])],"derivedFrom":makeQuery(id+"F1.opExtrude","CAP_FACE",FACE,{"disambiguationData":[OSD([subQ6,subQ8,subQ9,subQ7,subQ4,subQ3,subQ2,subQ1,subQ0,subQ5,subQ10,subQ11])],"isStart":true})});}
            var sketch = newSketch(context, id + "F16", { "sketchPlane" : qUnion([Q0])});
            skLineSegment(sketch, "E79", {"start": v(0, 90) * mm, "end": v(0, 120) * mm});
            skCircle(sketch, "E80", {"center": v(0, 120) * mm, "radius": 6 * mm});
            skLineSegment(sketch, "E81", {"start": v(-33, 90) * mm, "end": v(-15, 108) * mm});
            skLineSegment(sketch, "E82", {"start": v(-15, 108) * mm, "end": v(-15, 120) * mm});
            skLineSegment(sketch, "E83", {"start": v(33, 90) * mm, "end": v(15, 108) * mm});
            skLineSegment(sketch, "E84", {"start": v(15, 108) * mm, "end": v(15, 120) * mm});
            skArc(sketch, "E85", {"start": v(15, 120) * mm, "mid": v(0, 135) * mm, "end": v(-15, 120) * mm});
            skLineSegment(sketch, "E86", {"start": v(-80, 0) * mm, "end": v(80, 0) * mm, "construction": true});
            skLineSegment(sketch, "E87.MirrorCS", {"start": v(15, -108) * mm, "end": v(15, -120) * mm});
            skArc(sketch, "E88.MirrorCS", {"start": v(15, -120) * mm, "mid": v(0, -135) * mm, "end": v(-15, -120) * mm});
            skLineSegment(sketch, "E89.MirrorCS", {"start": v(33, -90) * mm, "end": v(15, -108) * mm});
            skLineSegment(sketch, "E90.MirrorCS", {"start": v(-15, -108) * mm, "end": v(-15, -120) * mm});
            skCircle(sketch, "E91.MirrorC", {"center": v(0, -120) * mm, "radius": 6 * mm});
            skLineSegment(sketch, "E92.MirrorCS", {"start": v(0, -90) * mm, "end": v(0, -120) * mm});
            skLineSegment(sketch, "E93.MirrorCS", {"start": v(-33, -90) * mm, "end": v(-15, -108) * mm});
            skSolve(sketch);
        }
        {
            var Q0;
            Q0=makeQuery(id+"F16.imprint","IMPRINT",FACE,{"disambiguationData":[TD([[makeQuery(id+"F16.imprint","IMPRINT",EDGE,{"derivedFrom":sQuery(id+"F16.wireOp",EDGE,"E80")}),-1.0]])]});
            var Q1;
            Q1=makeQuery(id+"F16.imprint","IMPRINT",FACE,{"disambiguationData":[TD([[makeQuery(id+"F16.imprint","IMPRINT",EDGE,{"derivedFrom":makeQuery(id+"F1.opExtrude","CAP_EDGE",EDGE,{"disambiguationData":[OSD([sQuery(id+"F0.wireOp",EDGE,"E1.left")])],"isStart":true})}),-1.0]])]});
            var Q2;
            Q2=makeQuery(id+"F16.imprint","IMPRINT",FACE,{"disambiguationData":[TD([[makeQuery(id+"F16.imprint","IMPRINT",EDGE,{"derivedFrom":sQuery(id+"F16.wireOp",EDGE,"E87.MirrorCS")}),-1.0]])]});
            var Q3;
            Q3 = qSketchRegion(id + "F0", true);
            var Q4;
            Q4=makeQuery(id+"F2.opExtrude","CAP_FACE",FACE,{"disambiguationData":[OSD([sQuery(id+"F0.wireOp",EDGE,"E12"),sQuery(id+"F0.wireOp",EDGE,"E13"),sQuery(id+"F0.wireOp",EDGE,"E14"),sQuery(id+"F0.wireOp",EDGE,"E15"),sQuery(id+"F0.wireOp",EDGE,"E17.filletArc"),sQuery(id+"F0.wireOp",EDGE,"E18.filletArc"),sQuery(id+"F0.wireOp",EDGE,"E19.filletArc"),sQuery(id+"F0.wireOp",EDGE,"E20.filletArc"),sQuery(id+"F0.wireOp",EDGE,"E25.0"),sQuery(id+"F0.wireOp",EDGE,"E25.1"),sQuery(id+"F0.wireOp",EDGE,"E25.2"),sQuery(id+"F0.wireOp",EDGE,"E25.3"),sQuery(id+"F0.wireOp",EDGE,"E25.4"),sQuery(id+"F0.wireOp",EDGE,"E25.5"),sQuery(id+"F0.wireOp",EDGE,"E25.6"),sQuery(id+"F0.wireOp",EDGE,"E25.7")])],"isStart":false});
            extrude(context, id + "F17", {"entities" : qUnion([Q0, Q1, Q2, Q3]), "endBound" : BoundingType.UP_TO_SURFACE, "endBoundEntityFace" : qUnion([Q4]), "depth" : 25 * mm});
        }
    });
